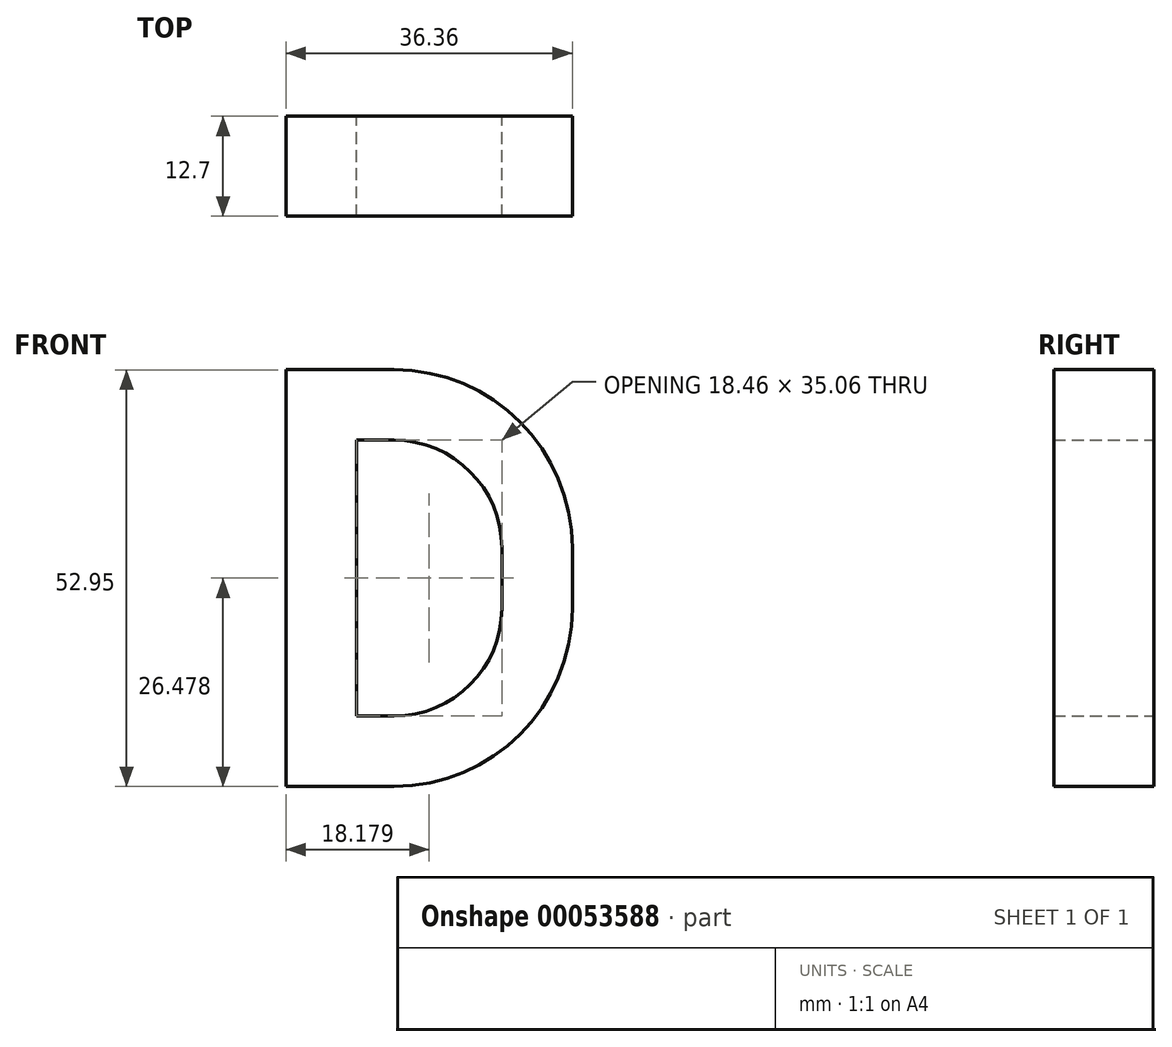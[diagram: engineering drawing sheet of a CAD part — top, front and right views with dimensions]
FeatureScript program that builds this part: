
annotation { "Feature Type Name" : "Feature", "Feature Type Description" : "" }
export const myFeature = defineFeature(function(context is Context, id is Id, definition is map)
    precondition{}
    {
        {
            var Q0;
            Q0=qCreatedBy(makeId("Front.planeOp"),FACE);
            var sketch = newSketch(context, id + "F0", { "sketchPlane" : qUnion([Q0])});
            skLineSegment(sketch, "E0", {"start": v(-52.2, 30.3) * mm, "end": v(-52.2, -22.65) * mm});
            skLineSegment(sketch, "E1", {"start": v(-52.2, 30.3) * mm, "end": v(-38.5, 30.3) * mm});
            skLineSegment(sketch, "E2", {"start": v(-52.2, -22.65) * mm, "end": v(-38.5, -22.65) * mm});
            skPoint(sketch, "E3", {"position": v(-52.2, 3.83) * mm});
            skLineSegment(sketch, "E4", {"start": v(-52.2, 3.83) * mm, "end": v(-15.85, 3.83) * mm});
            skLineSegment(sketch, "E5", {"start": v(-15.85, 3.83) * mm, "end": v(-15.85, 7.66) * mm});
            skLineSegment(sketch, "E6", {"start": v(-15.85, 3.83) * mm, "end": v(-15.85, 0) * mm});
            skArc(sketch, "E7", {"start": v(-15.85, 7.66) * mm, "mid": v(-22.49, 23.67) * mm, "end": v(-38.5, 30.3) * mm});
            skArc(sketch, "E8", {"start": v(-38.5, -22.65) * mm, "mid": v(-22.49, -16.01) * mm, "end": v(-15.85, 0) * mm});
            skLineSegment(sketch, "E9.0", {"start": v(-24.8, 3.83) * mm, "end": v(-24.8, 7.66) * mm});
            skLineSegment(sketch, "E9.1", {"start": v(-24.8, 3.83) * mm, "end": v(-24.8, 0) * mm});
            skLineSegment(sketch, "E9.2", {"start": v(-43.26, 21.36) * mm, "end": v(-38.5, 21.36) * mm});
            skLineSegment(sketch, "E9.3", {"start": v(-43.26, 21.36) * mm, "end": v(-43.26, -13.7) * mm});
            skLineSegment(sketch, "E9.4", {"start": v(-43.26, -13.7) * mm, "end": v(-38.5, -13.7) * mm});
            skArc(sketch, "E9.5", {"start": v(-24.8, 7.66) * mm, "mid": v(-28.81, 17.34) * mm, "end": v(-38.5, 21.36) * mm});
            skArc(sketch, "E9.6", {"start": v(-38.5, -13.7) * mm, "mid": v(-28.81, -9.69) * mm, "end": v(-24.8, 0) * mm});
            skSolve(sketch);
        }
        {
            var Q0;
            {var subQ7=sQuery(id+"F0.wireOp",EDGE,"E2");Q0=makeQuery(id+"F0.imprint","IMPRINT",FACE,{"disambiguationData":[TD([[makeQuery(id+"F0.imprint","IMPRINT",EDGE,{"derivedFrom":subQ7}),1.0]])]});}
            extrude(context, id + "F1", {"entities" : qUnion([Q0]), "depth" : 12.7 * mm});
        }
        {
            var Q0;
            Q0 = qSketchRegion(id + "F0", true);
            extrude(context, id + "F2", {"entities" : qUnion([Q0]), "operationType" : NewBodyOperationType.ADD, "depth" : 12.7 * mm});
        }
    });
